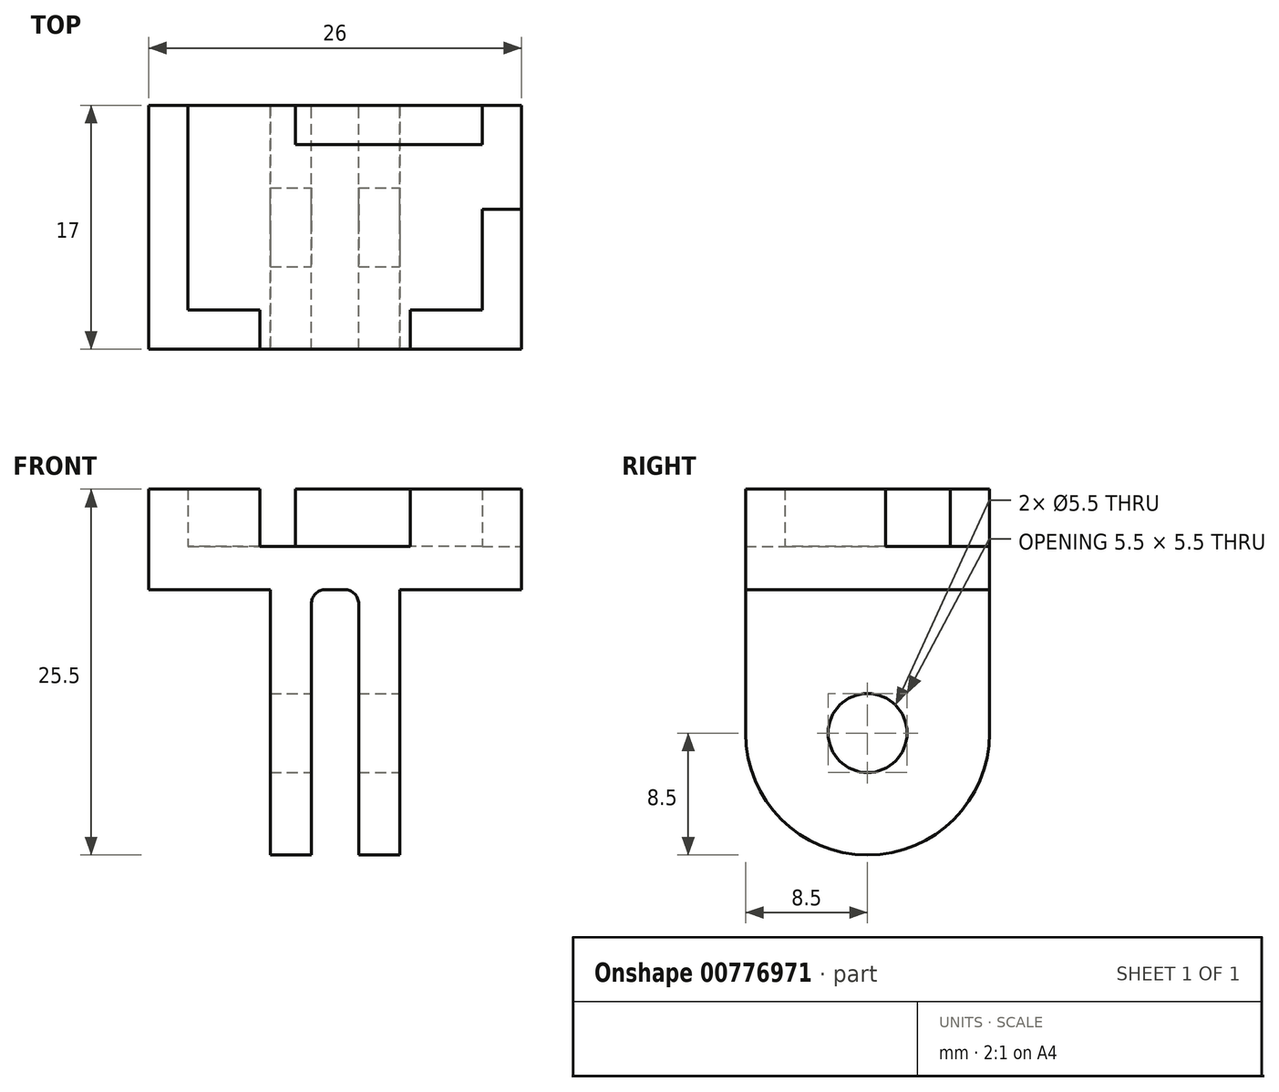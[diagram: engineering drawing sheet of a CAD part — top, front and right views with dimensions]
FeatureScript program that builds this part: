
annotation { "Feature Type Name" : "Feature", "Feature Type Description" : "" }
export const myFeature = defineFeature(function(context is Context, id is Id, definition is map)
    precondition{}
    {
        {
            var Q0;
            Q0=qCreatedBy(makeId("Top.planeOp"),FACE);
            var sketch = newSketch(context, id + "F0", { "sketchPlane" : qUnion([Q0])});
            skLineSegment(sketch, "E0.bottom", {"start": v(0, 0) * mm, "end": v(26, 0) * mm});
            skLineSegment(sketch, "E0.top", {"start": v(0, 17) * mm, "end": v(26, 17) * mm});
            skLineSegment(sketch, "E0.left", {"start": v(0, 0) * mm, "end": v(0, 17) * mm});
            skLineSegment(sketch, "E0.right", {"start": v(26, 0) * mm, "end": v(26, 17) * mm});
            skSolve(sketch);
        }
        {
            var Q0;
            Q0=qSketchRegion(id+"F0",true);
            extrude(context, id + "F1", {"entities" : qUnion([Q0]), "depth" : 3 * mm});
        }
        {
            var Q0;
            Q0=makeQuery(id+"F1.opExtrude","CAP_FACE",FACE,{"disambiguationData":[OSD([sQuery(id+"F0.wireOp",EDGE,"E0.bottom"),sQuery(id+"F0.wireOp",EDGE,"E0.top"),sQuery(id+"F0.wireOp",EDGE,"E0.left"),sQuery(id+"F0.wireOp",EDGE,"E0.right")])],"isStart":false});
            var sketch = newSketch(context, id + "F2", { "sketchPlane" : qUnion([Q0])});
            skLineSegment(sketch, "E1", {"start": v(26, 9.75) * mm, "end": v(23.25, 9.75) * mm});
            skLineSegment(sketch, "E2", {"start": v(23.25, 9.75) * mm, "end": v(23.25, 2.75) * mm});
            skLineSegment(sketch, "E3", {"start": v(23.25, 2.75) * mm, "end": v(18.25, 2.75) * mm});
            skLineSegment(sketch, "E4", {"start": v(18.25, 2.75) * mm, "end": v(18.25, 0) * mm});
            skPoint(sketch, "E4.endSnap0", {"position": v(13, 0) * mm});
            skLineSegment(sketch, "E5", {"start": v(18.25, 0) * mm, "end": v(26, 0) * mm});
            skLineSegment(sketch, "E6", {"start": v(26, 0) * mm, "end": v(26, 9.75) * mm});
            skLineSegment(sketch, "E7", {"start": v(23.25, 17) * mm, "end": v(23.25, 14.25) * mm});
            skLineSegment(sketch, "E8", {"start": v(23.25, 14.25) * mm, "end": v(10.25, 14.25) * mm});
            skLineSegment(sketch, "E9", {"start": v(10.25, 14.25) * mm, "end": v(10.25, 17) * mm});
            skLineSegment(sketch, "E10", {"start": v(10.25, 17) * mm, "end": v(23.25, 17) * mm});
            skLineSegment(sketch, "E11", {"start": v(0, 17) * mm, "end": v(0, 0) * mm});
            skLineSegment(sketch, "E12", {"start": v(0, 0) * mm, "end": v(7.75, 0) * mm});
            skLineSegment(sketch, "E13", {"start": v(7.75, 0) * mm, "end": v(7.75, 2.75) * mm});
            skLineSegment(sketch, "E14", {"start": v(7.75, 2.75) * mm, "end": v(2.75, 2.75) * mm});
            skLineSegment(sketch, "E15", {"start": v(2.75, 2.75) * mm, "end": v(2.75, 17) * mm});
            skLineSegment(sketch, "E16", {"start": v(2.75, 17) * mm, "end": v(0, 17) * mm});
            skSolve(sketch);
        }
        {
            var Q0;
            Q0=qSketchRegion(id+"F2",true);
            extrude(context, id + "F3", {"entities" : qUnion([Q0]), "operationType" : NewBodyOperationType.ADD, "depth" : 4 * mm});
        }
        {
            var Q0;
            Q0=makeQuery(id+"F1.opExtrude","CAP_EDGE",EDGE,{"disambiguationData":[OSD([sQuery(id+"F0.wireOp",EDGE,"E0.bottom")])],"isStart":true});
            cPoint(context, id + "F4", {"entities" : qUnion([Q0]), "parameter" : 0.5});
        }
        {
            var Q0;
            Q0=makeQuery(id+"F3.boolean.opBoolean","MERGE",FACE,{"derivedFrom":[makeQuery(id+"F1.opExtrude","SWEPT_FACE",FACE,{"disambiguationData":[OSD([sQuery(id+"F0.wireOp",EDGE,"E0.left")])]}),makeQuery(id+"F3.opExtrude","SWEPT_FACE",FACE,{"disambiguationData":[OSD([sQuery(id+"F2.wireOp",EDGE,"E11")])]})]});
            var Q1;
            Q1=qCreatedBy(id+"F4",VERTEX);
            cPlane(context, id + "F5", {"entities" : qUnion([Q0, Q1]), "cplaneType" : CPlaneType.PLANE_POINT, "offset" : 25 * mm, "width" : 150 * mm, "height" : 150 * mm});
        }
        {
            var Q0;
            Q0=qCreatedBy(id+"F5.planeOp",FACE);
            var sketch = newSketch(context, id + "F6", { "sketchPlane" : qUnion([Q0])});
            skLineSegment(sketch, "E17.bottom", {"start": v(0, 0) * mm, "end": v(-17, 0) * mm});
            skLineSegment(sketch, "E17.top", {"start": v(0, -10) * mm, "end": v(-17, -10) * mm});
            skLineSegment(sketch, "E17.left", {"start": v(0, 0) * mm, "end": v(0, -10) * mm});
            skLineSegment(sketch, "E17.right", {"start": v(-17, 0) * mm, "end": v(-17, -10) * mm});
            skCircle(sketch, "E18", {"center": v(-8.5, -10) * mm, "radius": 8.5 * mm});
            skCircle(sketch, "E19", {"center": v(-8.5, -10) * mm, "radius": 2.75 * mm});
            skSolve(sketch);
        }
        {
            var Q0;
            Q0=qSketchRegion(id+"F6",true);
            extrude(context, id + "F7", {"entities" : qUnion([Q0]), "operationType" : NewBodyOperationType.ADD, "depth" : 9 * mm, "symmetric" : true});
        }
        {
            var Q0;
            Q0=makeQuery(id+"F7.boolean.opBoolean","MERGE",FACE,{"derivedFrom":[makeQuery(id+"F3.boolean.opBoolean","MERGE",FACE,{"derivedFrom":[makeQuery(id+"F1.opExtrude","SWEPT_FACE",FACE,{"disambiguationData":[OSD([sQuery(id+"F0.wireOp",EDGE,"E0.top")])]}),makeQuery(id+"F3.opExtrude","SWEPT_FACE",FACE,{"disambiguationData":[OSD([sQuery(id+"F2.wireOp",EDGE,"E10")])]}),makeQuery(id+"F3.opExtrude","SWEPT_FACE",FACE,{"disambiguationData":[OSD([sQuery(id+"F2.wireOp",EDGE,"E16")])]})]}),makeQuery(id+"F7.opExtrude","SWEPT_FACE",FACE,{"disambiguationData":[OSD([sQuery(id+"F6.wireOp",EDGE,"E17.right")])]})]});
            var sketch = newSketch(context, id + "F8", { "sketchPlane" : qUnion([Q0])});
            skLineSegment(sketch, "E20.bottom", {"start": v(-11.35, 0) * mm, "end": v(-14.65, 0) * mm});
            skLineSegment(sketch, "E20.top", {"start": v(-11.35, -20.48) * mm, "end": v(-14.65, -20.48) * mm});
            skLineSegment(sketch, "E20.left", {"start": v(-11.35, 0) * mm, "end": v(-11.35, -20.48) * mm});
            skLineSegment(sketch, "E20.right", {"start": v(-14.65, 0) * mm, "end": v(-14.65, -20.48) * mm});
            skSolve(sketch);
        }
        {
            var Q0;
            Q0=qSketchRegion(id+"F8",true);
            extrude(context, id + "F9", {"entities" : qUnion([Q0]), "operationType" : NewBodyOperationType.REMOVE, "oppositeDirection" : true, "depth" : 25 * mm});
        }
        {
            var Q0;
            Q0=makeQuery(id+"F3.opExtrude","CAP_EDGE",EDGE,{"disambiguationData":[OSD([sQuery(id+"F2.wireOp",EDGE,"E3")])],"isStart":true});
            var Q1;
            Q1=makeQuery(id+"F3.opExtrude","CAP_EDGE",EDGE,{"disambiguationData":[OSD([sQuery(id+"F2.wireOp",EDGE,"E14")])],"isStart":true});
            var Q2;
            Q2=makeQuery(id+"F7.opExtrude","CAP_EDGE",EDGE,{"disambiguationData":[OSD([sQuery(id+"F6.wireOp",EDGE,"E17.bottom")])],"isStart":false});
            var Q3;
            Q3=makeQuery(id+"F7.opExtrude","CAP_EDGE",EDGE,{"disambiguationData":[OSD([sQuery(id+"F6.wireOp",EDGE,"E17.bottom")])],"isStart":true});
            var Q4;
            Q4=makeQuery(id+"F9.boolean.opBoolean","COPY",EDGE,{"derivedFrom":makeQuery(id+"F9.opExtrude","SWEPT_EDGE",EDGE,{"disambiguationData":[OSD([sQuery(id+"F8.wireOp",EDGE,"E20.bottom"),sQuery(id+"F8.wireOp",EDGE,"E20.right")])]})});
            var Q5;
            Q5=makeQuery(id+"F9.boolean.opBoolean","COPY",EDGE,{"derivedFrom":makeQuery(id+"F9.opExtrude","SWEPT_EDGE",EDGE,{"disambiguationData":[OSD([sQuery(id+"F8.wireOp",EDGE,"E20.bottom"),sQuery(id+"F8.wireOp",EDGE,"E20.left")])]})});
            fillet(context, id + "F10", {"entities" : qUnion([Q0, Q1, Q2, Q3, Q4, Q5]), "radius" : 1 * mm, "tangentPropagation" : true, "allowEdgeOverflow" : false});
        }
    });
